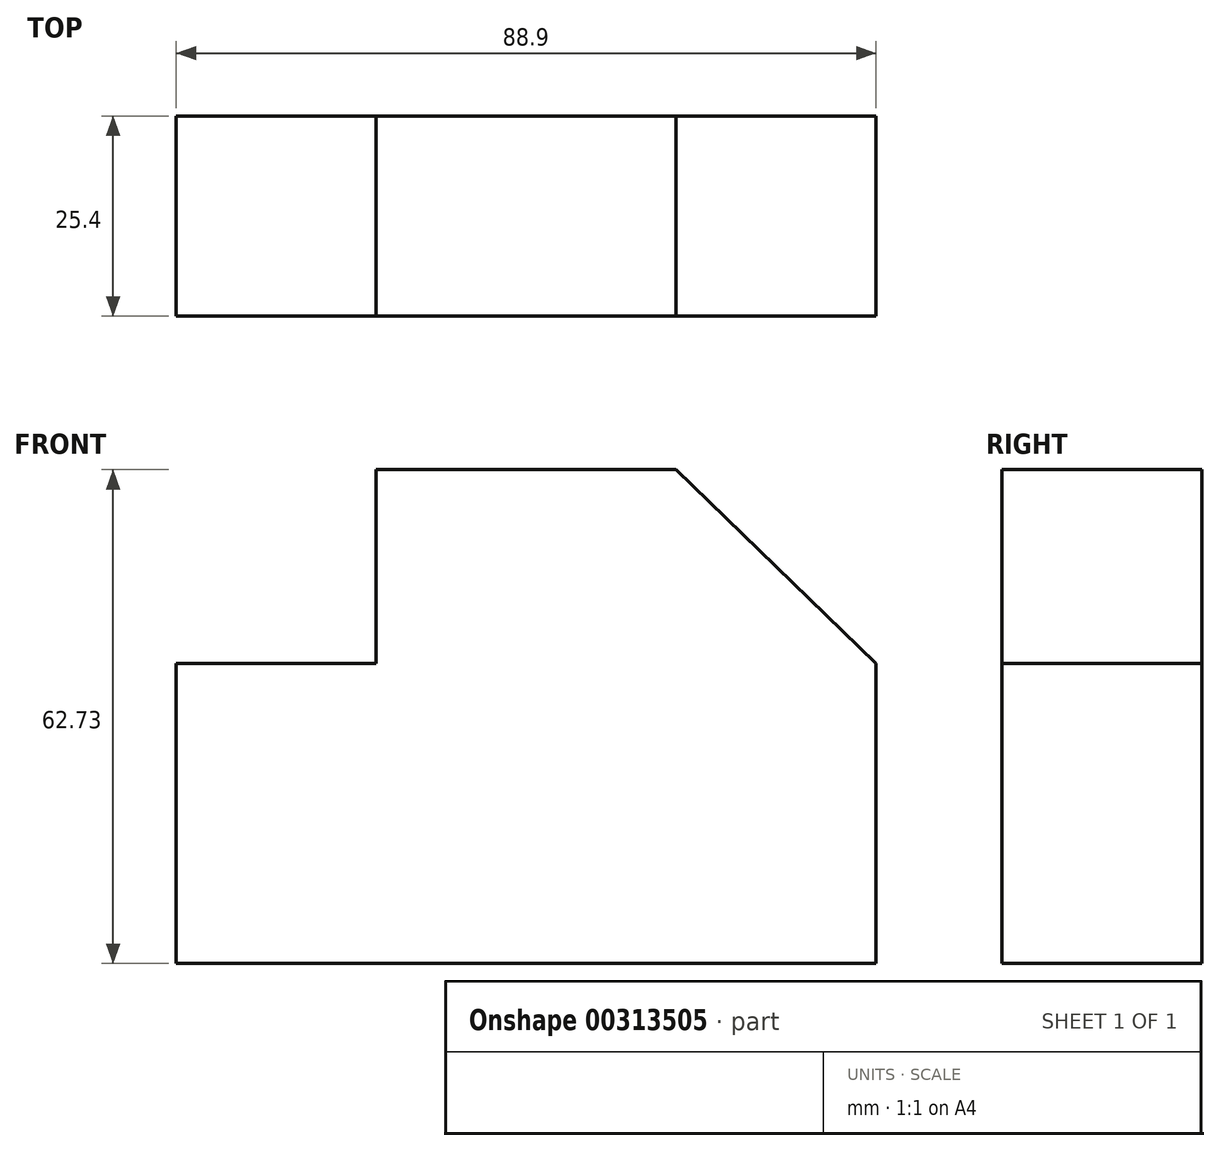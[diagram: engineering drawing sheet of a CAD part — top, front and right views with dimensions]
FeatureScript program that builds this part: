
annotation { "Feature Type Name" : "Feature", "Feature Type Description" : "" }
export const myFeature = defineFeature(function(context is Context, id is Id, definition is map)
    precondition{}
    {
        {
            var Q0;
            Q0=qCreatedBy(makeId("Front.planeOp"),FACE);
            var sketch = newSketch(context, id + "F0", { "sketchPlane" : qUnion([Q0])});
            skLineSegment(sketch, "E0", {"start": v(-33.83, -19.13) * mm, "end": v(55.07, -19.13) * mm});
            skLineSegment(sketch, "E1", {"start": v(-33.83, -19.13) * mm, "end": v(-33.83, 18.97) * mm});
            skLineSegment(sketch, "E2", {"start": v(-33.83, 18.97) * mm, "end": v(-8.43, 18.97) * mm});
            skLineSegment(sketch, "E3", {"start": v(-8.43, 18.97) * mm, "end": v(-8.43, 43.6) * mm});
            skLineSegment(sketch, "E4", {"start": v(-8.43, 43.6) * mm, "end": v(29.67, 43.6) * mm});
            skLineSegment(sketch, "E5", {"start": v(55.07, -19.13) * mm, "end": v(55.07, 18.97) * mm});
            skLineSegment(sketch, "E6", {"start": v(29.67, 43.6) * mm, "end": v(55.07, 18.97) * mm});
            skSolve(sketch);
        }
        {
            var Q0;
            Q0 = qSketchRegion(id + "F0", true);
            extrude(context, id + "F1", {"entities" : qUnion([Q0]), "oppositeDirection" : true, "depth" : 25.4 * mm});
        }
    });
